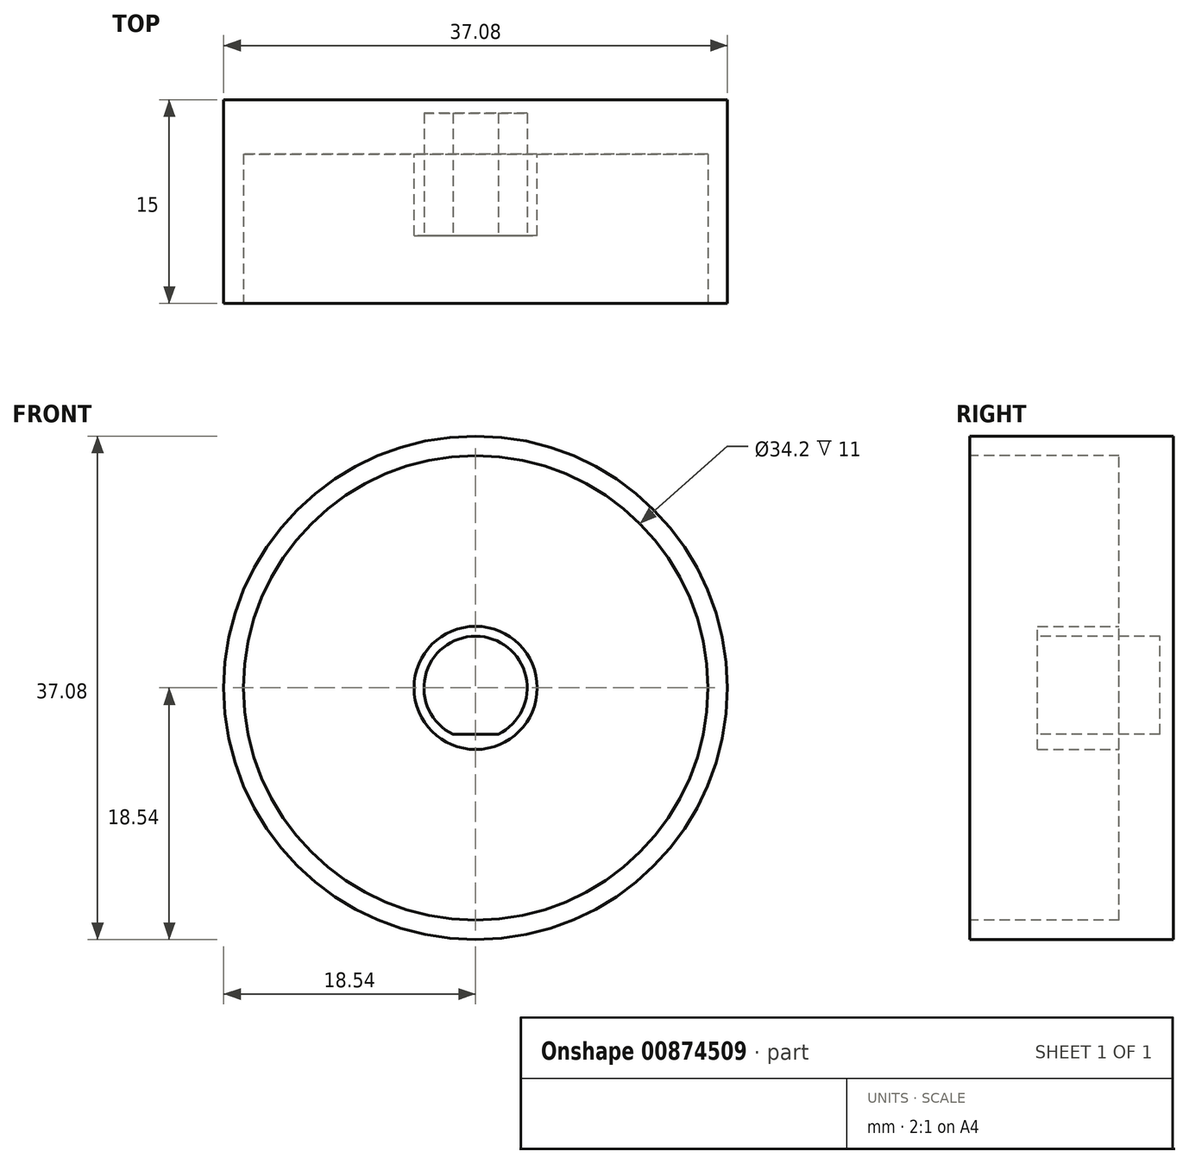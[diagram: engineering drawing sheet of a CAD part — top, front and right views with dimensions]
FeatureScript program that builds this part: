
annotation { "Feature Type Name" : "Feature", "Feature Type Description" : "" }
export const myFeature = defineFeature(function(context is Context, id is Id, definition is map)
    precondition{}
    {
        {
            var Q0;
            Q0=qCreatedBy(makeId("Front.planeOp"),FACE);
            var sketch = newSketch(context, id + "F0", { "sketchPlane" : qUnion([Q0])});
            skCircle(sketch, "E0", {"center": v(0, 0) * mm, "radius": 18.54 * mm});
            skCircle(sketch, "E1", {"center": v(0, 0) * mm, "radius": 4.54 * mm});
            skLineSegment(sketch, "E2", {"start": v(-2.5, -3.78) * mm, "end": v(2.5, -3.78) * mm});
            skSolve(sketch);
        }
        {
            var Q0;
            Q0=makeQuery(id+"F0.imprint","IMPRINT",FACE,{"disambiguationData":[TD([[makeQuery(id+"F0.imprint","IMPRINT",EDGE,{"derivedFrom":sQuery(id+"F0.wireOp",EDGE,"E0")}),1.0]])]});
            var Q1;
            {var subQ0=sQuery(id+"F0.wireOp",EDGE,"E2");Q1=makeQuery(id+"F0.imprint","IMPRINT",FACE,{"disambiguationData":[TD([[makeQuery(id+"F0.imprint","IMPRINT",EDGE,{"derivedFrom":subQ0}),1.0]])]});}
            var Q2;
            {var subQ0=sQuery(id+"F0.wireOp",EDGE,"E2");Q2=makeQuery(id+"F0.imprint","IMPRINT",FACE,{"disambiguationData":[TD([[makeQuery(id+"F0.imprint","IMPRINT",EDGE,{"derivedFrom":subQ0}),-1.0]])]});}
            extrude(context, id + "F1", {"entities" : qUnion([Q0, Q1, Q2]), "depth" : 15 * mm, "offsetDistance" : 25 * mm});
        }
        {
            var Q0;
            Q0=makeQuery(id+"F1.opExtrude","CAP_FACE",FACE,{"disambiguationData":[OSD([sQuery(id+"F0.wireOp",EDGE,"E0")])],"isStart":false});
            var sketch = newSketch(context, id + "F2", { "sketchPlane" : qUnion([Q0])});
            skCircle(sketch, "E3", {"center": v(0, 0) * mm, "radius": 17.1 * mm});
            skSolve(sketch);
        }
        {
            var Q0;
            Q0=makeQuery(id+"F2.imprint","IMPRINT",FACE,{"disambiguationData":[TD([[makeQuery(id+"F2.imprint","IMPRINT",EDGE,{"derivedFrom":sQuery(id+"F2.wireOp",EDGE,"E3")}),1.0]])]});
            extrude(context, id + "F3", {"entities" : qUnion([Q0]), "operationType" : NewBodyOperationType.REMOVE, "oppositeDirection" : true, "depth" : 11 * mm, "offsetDistance" : 25 * mm});
        }
        {
            var Q0;
            Q0=makeQuery(id+"F3.boolean.opBoolean","COPY",FACE,{"derivedFrom":makeQuery(id+"F3.opExtrude","CAP_FACE",FACE,{"disambiguationData":[OSD([sQuery(id+"F2.wireOp",EDGE,"E3")])],"isStart":false})});
            var sketch = newSketch(context, id + "F4", { "sketchPlane" : qUnion([Q0])});
            skSolve(sketch);
        }
        {
            var Q0;
            Q0=makeQuery(id+"F4.imprint","IMPRINT",FACE,{"disambiguationData":[TD([[makeQuery(id+"F4.imprint","IMPRINT",EDGE,{"derivedFrom":makeQuery(id+"F3.boolean.opBoolean","COPY",EDGE,{"derivedFrom":makeQuery(id+"F3.opExtrude","CAP_EDGE",EDGE,{"disambiguationData":[OSD([sQuery(id+"F2.wireOp",EDGE,"E3")])],"isStart":false})})}),1.0]])]});
            var sketch = newSketch(context, id + "F5", { "sketchPlane" : qUnion([Q0])});
            skCircle(sketch, "E4", {"center": v(0, 0) * mm, "radius": 4.54 * mm});
            skSolve(sketch);
        }
        {
            var Q0;
            Q0=makeQuery(id+"F5.imprint","IMPRINT",FACE,{"disambiguationData":[TD([[makeQuery(id+"F5.imprint","IMPRINT",EDGE,{"derivedFrom":sQuery(id+"F5.wireOp",EDGE,"E4")}),1.0]])]});
            extrude(context, id + "F6", {"entities" : qUnion([Q0]), "operationType" : NewBodyOperationType.ADD, "depth" : 6 * mm, "offsetDistance" : 25 * mm});
        }
        {
            var Q0;
            Q0=makeQuery(id+"F6.opExtrude","CAP_FACE",FACE,{"disambiguationData":[OSD([sQuery(id+"F5.wireOp",EDGE,"E4")])],"isStart":false});
            var sketch = newSketch(context, id + "F7", { "sketchPlane" : qUnion([Q0])});
            skSolve(sketch);
        }
        {
            var Q0;
            Q0=makeQuery(id+"F7.imprint","IMPRINT",FACE,{"disambiguationData":[TD([[makeQuery(id+"F7.imprint","IMPRINT",EDGE,{"derivedFrom":makeQuery(id+"F6.opExtrude","CAP_EDGE",EDGE,{"disambiguationData":[OSD([sQuery(id+"F5.wireOp",EDGE,"E4")])],"isStart":false})}),1.0]])]});
            var sketch = newSketch(context, id + "F8", { "sketchPlane" : qUnion([Q0])});
            skCircle(sketch, "E5", {"center": v(0, 0) * mm, "radius": 3.8 * mm});
            skLineSegment(sketch, "E6", {"start": v(-1.66, -3.42) * mm, "end": v(1.66, -3.42) * mm});
            skSolve(sketch);
        }
        {
            var Q0;
            {var subQ0=sQuery(id+"F8.wireOp",EDGE,"E6");Q0=makeQuery(id+"F8.imprint","IMPRINT",FACE,{"disambiguationData":[TD([[makeQuery(id+"F8.imprint","IMPRINT",EDGE,{"derivedFrom":subQ0}),1.0]])]});}
            extrude(context, id + "F9", {"entities" : qUnion([Q0]), "operationType" : NewBodyOperationType.REMOVE, "oppositeDirection" : true, "depth" : 9 * mm, "offsetDistance" : 25 * mm});
        }
    });
